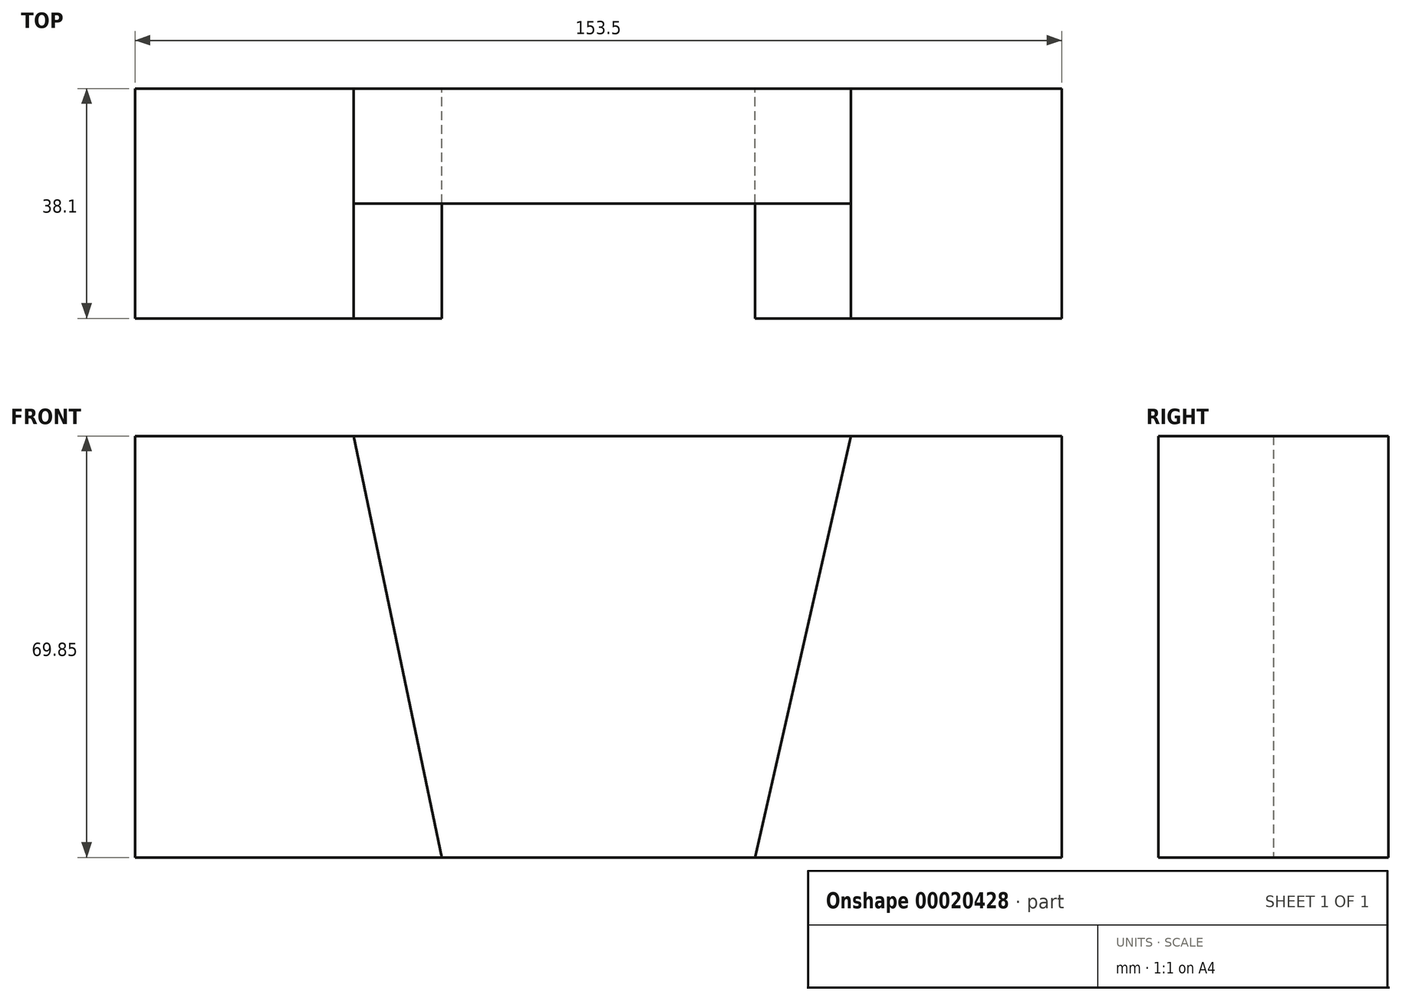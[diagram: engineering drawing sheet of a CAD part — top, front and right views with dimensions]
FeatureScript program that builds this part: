
annotation { "Feature Type Name" : "Feature", "Feature Type Description" : "" }
export const myFeature = defineFeature(function(context is Context, id is Id, definition is map)
    precondition{}
    {
        {
            var Q0;
            Q0=qCreatedBy(makeId("Front.planeOp"),FACE);
            var sketch = newSketch(context, id + "F0", { "sketchPlane" : qUnion([Q0])});
            skLineSegment(sketch, "E0.left", {"start": v(-125.57, 25.24) * mm, "end": v(-125.57, -44.6) * mm});
            skLineSegment(sketch, "E0.right", {"start": v(27.93, 25.24) * mm, "end": v(27.93, -44.6) * mm});
            skLineSegment(sketch, "E1", {"start": v(-125.57, 25.24) * mm, "end": v(-89.37, 25.24) * mm});
            skLineSegment(sketch, "E2", {"start": v(-125.57, -44.6) * mm, "end": v(-74.77, -44.6) * mm});
            skLineSegment(sketch, "E3", {"start": v(-89.37, 25.24) * mm, "end": v(-74.77, -44.6) * mm});
            skPoint(sketch, "E4", {"position": v(-7, 25.24) * mm});
            skLineSegment(sketch, "E5", {"start": v(27.93, 25.24) * mm, "end": v(-7, 25.24) * mm});
            skLineSegment(sketch, "E6", {"start": v(27.93, -44.6) * mm, "end": v(-22.87, -44.6) * mm});
            skLineSegment(sketch, "E7", {"start": v(-7, 25.24) * mm, "end": v(-22.87, -44.6) * mm});
            skLineSegment(sketch, "E8", {"start": v(-89.37, 25.24) * mm, "end": v(-7, 25.24) * mm});
            skLineSegment(sketch, "E9", {"start": v(-74.77, -44.6) * mm, "end": v(-22.87, -44.6) * mm});
            skSolve(sketch);
        }
        {
            var Q0;
            Q0=makeQuery(id+"F0.imprint","IMPRINT",FACE,{"disambiguationData":[TD([[makeQuery(id+"F0.imprint","IMPRINT",EDGE,{"derivedFrom":sQuery(id+"F0.wireOp",EDGE,"E0.right")}),-1.0]])]});
            var Q1;
            Q1=makeQuery(id+"F0.imprint","IMPRINT",FACE,{"disambiguationData":[TD([[makeQuery(id+"F0.imprint","IMPRINT",EDGE,{"derivedFrom":sQuery(id+"F0.wireOp",EDGE,"E0.left")}),1.0]])]});
            extrude(context, id + "F1", {"entities" : qUnion([Q0, Q1]), "depth" : 38.1 * mm});
        }
        {
            var Q0;
            Q0=makeQuery(id+"F0.imprint","IMPRINT",FACE,{"disambiguationData":[TD([[makeQuery(id+"F0.imprint","IMPRINT",EDGE,{"derivedFrom":sQuery(id+"F0.wireOp",EDGE,"E3")}),1.0]])]});
            extrude(context, id + "F2", {"entities" : qUnion([Q0]), "depth" : 19.05 * mm});
        }
    });
